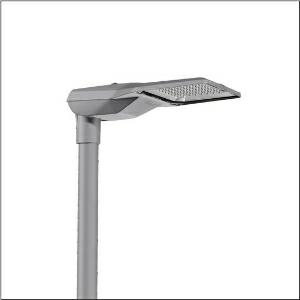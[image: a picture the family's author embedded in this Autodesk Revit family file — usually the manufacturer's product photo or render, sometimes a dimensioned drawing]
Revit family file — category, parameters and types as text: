
# Revit family: streetlight_sl_21_midi___st1_5a_5xe3p43s08lb_fbc0
name_source: partatom
category: Lighting Fixtures
units: mm (PartAtom-declared; Revit-internal decimal feet)

## family parameters
Cut with Voids When Loaded = No
Host = Face
Light Source = No
Part Type = Normal
Room Calculation Point = No
Round Connector Dimension = Use Diameter
Shared = No

## types (1)
- --- (1 x LED, 14690 lm, 99.6 W, 4000K)
    Apparent Load = 100 VA
    CIE Flux Codes = 22 53 95 100 100
    Color Rendering = 70
    Color Temperature = 4000K
    Default Elevation = 1800 mm
    Description = Streetlight SL 21 midi, mast luminaire, primary light control with lens, of PMMA, primary optical cover: cover, of toughened safety glass, transparent, light distribution: ST1.5a, light emission: direct distribution, primary light characteristic: asymmetric, installation type: side-entry, post-top, LED, High Power LED, rated luminous flux: 14.690lm, luminous efficacy: 148lm/W, light colour: 740, colour temperature: 4000K, control gear: D4i, control: overheat protection, constant luminous flux control, time-dependent luminous flux control, flexible luminous flux parameterisation, pre-setting: logarithmic dimming characteristic, mains connection: 230..240V, AC, 50/60Hz, start of lifetime: 100W, end of service life: 102W, reduction: 46W, luminaire housing, of diecast aluminium, powder-coated, SITECO metallic grey (DB 702S), corrosivity category C5 high according to DIN EN ISO 12944, please order mast flange separately, inclination adjustable: 0°, 5°, 10°, 15°, sealing non-destructively replaceable, multi-level sealing system, length: 644mm, width: 335mm, height: 110mm, mast flange for spigot size: 42mm (side-entry): 5XC10008XM4, 60/48mm (side-entry/post-top): 5XC10108XM2, 76/60mm (side-entry/post-top): 5XC10108XM1, mounting height: 4..8m, Smart Interface above, protection rating (complete): IP66, insulation class (complete): insulation class II (safety insulation), certification: CE, ENEC, ENEC+, VDE, impact resistance: IK10, permissible operating ambient temperature for outdoor applications: -40..+50°C, standard-compliant lighting for roads and squares, packaging unit: 1 piece

Light Distribution: ST1.5a
    Height = 111 mm
    Lamp = 1 x LED
    Lamp Light Flux = 14690 lm
    Lamp Power = 99.6 W
    Lamp count = 1
    Length = 644 mm
    Luminous efficacy = 147 lm/W
    Manufacturer = Siteco
    ModVariant = No
    Model = 5XE3P43S08LB
    Number of Poles = 1
    OnlyDefault = Yes
    Power Factor = 1
    Product Name = Streetlight SL 21 midi | ST1.5a
    Product group = mast luminaire | pylon top
    ProductGroupID = 6100
    Protection Class = Protection class II
    Protection Degree = IP 66
    RLX_Detail_Level = 1
    RLX_Emergency_Light_Flux = 0 lm
    RLX_Emergency_Type = 0
    RLX_Emergency_Type_DB = No
    RlxData = <blob elided: 30317 chars, md5=e4044182>
    Socket = socket
    Standby Power = 0 W
    System Light Flux = 14690 lm
    System Power = 100 W
    Type Comments = factory setting: luminous flux: 100 % | dim-lin: 254 | 1020 mA
    Type Image = l_1004302.jpg
    URL = http://relux.com
    VarID = @adj_032453
    Voltage = 0 V
    Weight = 0.00 kg
    Width = 336 mm

## geometry (parser evidence)
native form markers: Blend x4, Sweep x11
no freeform markers — native parametric forms only
